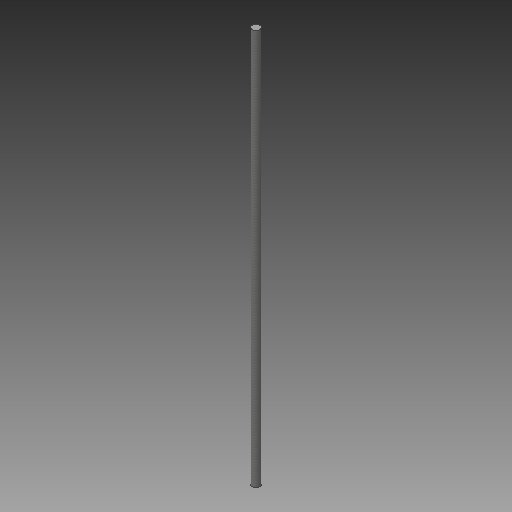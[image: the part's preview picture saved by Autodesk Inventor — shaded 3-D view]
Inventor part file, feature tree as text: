
AUTODESK INVENTOR PART (.ipt)
format: ipt  version: 2019 (Build 230136000, 136)  size: 99,840 bytes
history: native  units: in
note: dims shown in document units (in); Inventor stores cm internally (conversion verified against a paired STEP export)
features: extrude x1, thread x1, sketch x1
ambient origin geometry x8: Origin, YZ Plane, XZ Plane, XY Plane, X Axis, Y Axis, Z Axis, Center Point
bodies: Solid1 (feature_tree)
feature tree (3):
  extrude  "Extrusion1"  Depth=12.0in TaperAngle=0.0deg
  thread  "Thread2"  [1 undecoded]
  sketch  "Sketch1"  dims[d0=0.2362in d1=12.0in d2=0.0in d5=0.3937in d6=0.0in]
note: 1 required parameter value undecoded (feature->parameter linkage not recoverable at this tier; creation-order binding heuristic only, values carry confidence <= 0.55)
